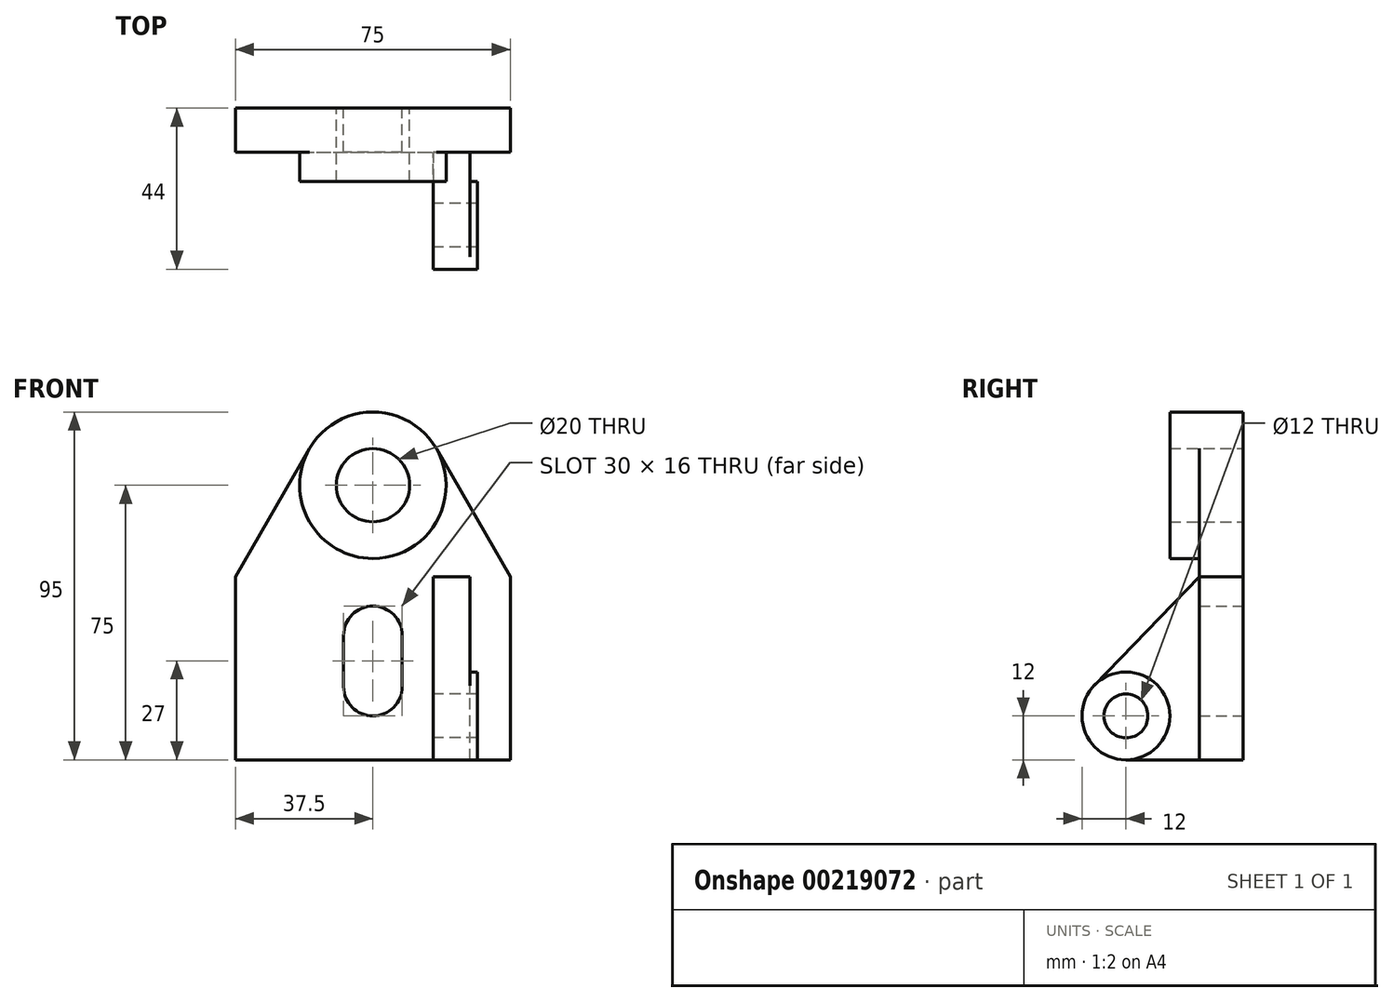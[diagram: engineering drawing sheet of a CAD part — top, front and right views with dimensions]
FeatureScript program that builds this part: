
annotation { "Feature Type Name" : "Feature", "Feature Type Description" : "" }
export const myFeature = defineFeature(function(context is Context, id is Id, definition is map)
    precondition{}
    {
        {
            var Q0;
            Q0=qCreatedBy(makeId("Front.planeOp"),FACE);
            var sketch = newSketch(context, id + "F0", { "sketchPlane" : qUnion([Q0])});
            skCircle(sketch, "E0", {"center": v(0, 75) * mm, "radius": 20 * mm});
            skCircle(sketch, "E1", {"center": v(0, 75) * mm, "radius": 10 * mm});
            skLineSegment(sketch, "E2", {"start": v(-37.5, 0) * mm, "end": v(37.5, 0) * mm});
            skLineSegment(sketch, "E3", {"start": v(37.5, 0) * mm, "end": v(37.5, 50) * mm});
            skLineSegment(sketch, "E4", {"start": v(-37.5, 50) * mm, "end": v(-37.5, 0) * mm});
            skLineSegment(sketch, "E5", {"start": v(-37.5, 50) * mm, "end": v(-17.33, 84.99) * mm});
            skLineSegment(sketch, "E6", {"start": v(37.5, 50) * mm, "end": v(17.33, 84.99) * mm});
            skArc(sketch, "E7", {"start": v(-8, 20) * mm, "mid": v(0, 12) * mm, "end": v(8, 20) * mm});
            skArc(sketch, "E8", {"start": v(8, 34) * mm, "mid": v(0, 42) * mm, "end": v(-8, 34) * mm});
            skLineSegment(sketch, "E9", {"start": v(8, 34) * mm, "end": v(8, 20) * mm});
            skLineSegment(sketch, "E10", {"start": v(-8, 34) * mm, "end": v(-8, 20) * mm});
            skSolve(sketch);
        }
        {
            var Q0;
            Q0=makeQuery(id+"F0.imprint","IMPRINT",FACE,{"disambiguationData":[TD([[makeQuery(id+"F0.imprint","IMPRINT",EDGE,{"derivedFrom":sQuery(id+"F0.wireOp",EDGE,"E2")}),1.0]])]});
            extrude(context, id + "F1", {"entities" : qUnion([Q0]), "depth" : 12 * mm});
        }
        {
            var Q0;
            Q0=makeQuery(id+"F0.imprint","IMPRINT",FACE,{"disambiguationData":[TD([[makeQuery(id+"F0.imprint","IMPRINT",EDGE,{"derivedFrom":sQuery(id+"F0.wireOp",EDGE,"E1")}),-1.0]])]});
            extrude(context, id + "F2", {"entities" : qUnion([Q0]), "operationType" : NewBodyOperationType.ADD, "depth" : 20 * mm});
        }
        {
            var Q0;
            Q0=qCreatedBy(makeId("Right.planeOp"),FACE);
            cPlane(context, id + "F3", {"entities" : qUnion([Q0]), "cplaneType" : CPlaneType.OFFSET, "offset" : (33 / 2) * mm, "width" : 150 * mm, "height" : 150 * mm});
        }
        {
            var Q0;
            Q0=qCreatedBy(id+"F3.planeOp",FACE);
            var sketch = newSketch(context, id + "F4", { "sketchPlane" : qUnion([Q0])});
            skCircle(sketch, "E11", {"center": v(-32, 12) * mm, "radius": 6 * mm});
            skCircle(sketch, "E12", {"center": v(-32, 12) * mm, "radius": 12 * mm});
            skPoint(sketch, "E13.0", {"position": v(-12, 50) * mm});
            skPoint(sketch, "E14.0", {"position": v(-12, 0) * mm});
            skLineSegment(sketch, "E15", {"start": v(-12, 50) * mm, "end": v(-40.63, 20.33) * mm});
            skLineSegment(sketch, "E16", {"start": v(-32, 0) * mm, "end": v(-12, 0) * mm});
            skPoint(sketch, "E17.orphan", {"position": v(-60.26, 0) * mm});
            skLineSegment(sketch, "E18", {"start": v(-12, 50) * mm, "end": v(-12, 0) * mm});
            skPoint(sketch, "E19.orphan", {"position": v(-12, 63.7) * mm});
            skSolve(sketch);
        }
        {
            var Q0;
            {var subQ0=sQuery(id+"F4.wireOp",EDGE,"E15");Q0=makeQuery(id+"F4.imprint","IMPRINT",FACE,{"disambiguationData":[TD([[makeQuery(id+"F4.imprint","IMPRINT",EDGE,{"derivedFrom":subQ0}),1.0]])]});}
            extrude(context, id + "F5", {"entities" : qUnion([Q0]), "operationType" : NewBodyOperationType.ADD, "depth" : 10 * mm});
        }
        {
            var Q0;
            Q0=makeQuery(id+"F4.imprint","IMPRINT",FACE,{"disambiguationData":[TD([[makeQuery(id+"F4.imprint","IMPRINT",EDGE,{"derivedFrom":sQuery(id+"F4.wireOp",EDGE,"E11")}),-1.0]])]});
            extrude(context, id + "F6", {"entities" : qUnion([Q0]), "operationType" : NewBodyOperationType.ADD, "depth" : 12 * mm});
        }
    });
